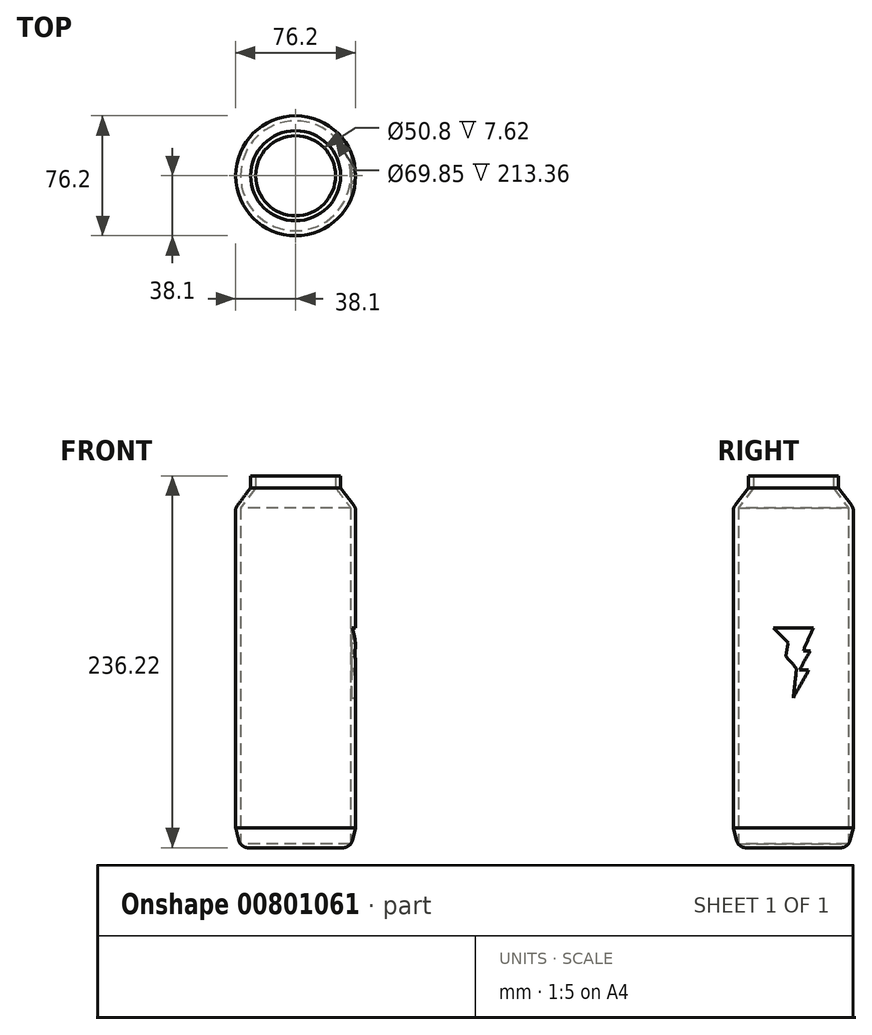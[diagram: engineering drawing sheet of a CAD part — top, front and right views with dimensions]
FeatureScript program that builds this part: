
annotation { "Feature Type Name" : "Feature", "Feature Type Description" : "" }
export const myFeature = defineFeature(function(context is Context, id is Id, definition is map)
    precondition{}
    {
        {
            var Q0;
            Q0=qCreatedBy(makeId("Top.planeOp"),FACE);
            var sketch = newSketch(context, id + "F0", { "sketchPlane" : qUnion([Q0])});
            skCircle(sketch, "E0", {"center": v(0, 0) * mm, "radius": 34.93 * mm});
            skCircle(sketch, "E1", {"center": v(0, 0) * mm, "radius": 38.1 * mm});
            skSolve(sketch);
        }
        {
            var Q0;
            Q0=makeQuery(id+"F0.imprint","IMPRINT",FACE,{"disambiguationData":[TD([[makeQuery(id+"F0.imprint","IMPRINT",EDGE,{"derivedFrom":sQuery(id+"F0.wireOp",EDGE,"E0")}),-1.0]])]});
            extrude(context, id + "F1", {"entities" : qUnion([Q0]), "depth" : 203.2 * mm, "offsetDistance" : 25.4 * mm});
        }
        {
            var Q0;
            Q0=makeQuery(id+"F0.imprint","IMPRINT",FACE,{"disambiguationData":[TD([[makeQuery(id+"F0.imprint","IMPRINT",EDGE,{"derivedFrom":sQuery(id+"F0.wireOp",EDGE,"E0")}),-1.0]])]});
            cPlane(context, id + "F2", {"entities" : qUnion([Q0]), "cplaneType" : CPlaneType.OFFSET, "offset" : 12.7 * mm, "oppositeDirection" : true, "width" : 152.4 * mm, "height" : 152.4 * mm});
        }
        {
            var Q0;
            Q0=qCreatedBy(id+"F2.planeOp",FACE);
            var sketch = newSketch(context, id + "F3", { "sketchPlane" : qUnion([Q0])});
            skCircle(sketch, "E2", {"center": v(0, 0) * mm, "radius": 34.93 * mm});
            skSolve(sketch);
        }
        {
            var Q0;
            Q0=qCreatedBy(makeId("Front.planeOp"),FACE);
            var sketch = newSketch(context, id + "F4", { "sketchPlane" : qUnion([Q0])});
            skLineSegment(sketch, "E3", {"start": v(-34.93, -12.7) * mm, "end": v(-38.1, 0) * mm});
            skLineSegment(sketch, "E4", {"start": v(-34.93, -12.7) * mm, "end": v(-34.93, 0) * mm});
            skLineSegment(sketch, "E5", {"start": v(-34.93, 0) * mm, "end": v(-38.1, 0) * mm});
            skSolve(sketch);
        }
        {
            var Q0;
            Q0=qCreatedBy(makeId("Front.planeOp"),FACE);
            var sketch = newSketch(context, id + "F5", { "sketchPlane" : qUnion([Q0])});
            skLineSegment(sketch, "E6", {"start": v(0, 0) * mm, "end": v(0, -12.7) * mm});
            skSolve(sketch);
        }
        {
            var Q0;
            Q0 = qSketchRegion(id + "F4", true);
            var Q1;
            Q1=sQuery(id+"F5.wireOp",EDGE,"E6");
            revolve(context, id + "F6", {"operationType" : NewBodyOperationType.ADD, "surfaceOperationType" : NewSurfaceOperationType.NEW, "entities" : qUnion([Q0]), "axis" : qUnion([Q1]), "revolveType" : RevolveType.FULL});
        }
        {
            var Q0;
            Q0=makeQuery(id+"F3.imprint","IMPRINT",FACE,{"disambiguationData":[TD([[makeQuery(id+"F3.imprint","IMPRINT",EDGE,{"derivedFrom":sQuery(id+"F3.wireOp",EDGE,"E2")}),1.0]])]});
            extrude(context, id + "F7", {"entities" : qUnion([Q0]), "operationType" : NewBodyOperationType.ADD, "depth" : 2.54 * mm, "offsetDistance" : 25.4 * mm});
        }
        {
            var Q0;
            Q0=makeQuery(id+"F1.opExtrude","CAP_FACE",FACE,{"disambiguationData":[OSD([sQuery(id+"F0.wireOp",EDGE,"E0"),sQuery(id+"F0.wireOp",EDGE,"E1")])],"isStart":false});
            cPlane(context, id + "F8", {"entities" : qUnion([Q0]), "cplaneType" : CPlaneType.OFFSET, "offset" : 12.7 * mm, "width" : 152.4 * mm, "height" : 152.4 * mm});
        }
        {
            var Q0;
            Q0=qCreatedBy(id+"F8.planeOp",FACE);
            var sketch = newSketch(context, id + "F9", { "sketchPlane" : qUnion([Q0])});
            skCircle(sketch, "E7", {"center": v(0, 0) * mm, "radius": 28.58 * mm});
            skSolve(sketch);
        }
        {
            var Q0;
            Q0=qCreatedBy(id+"F8.planeOp",FACE);
            var sketch = newSketch(context, id + "F10", { "sketchPlane" : qUnion([Q0])});
            skCircle(sketch, "E8", {"center": v(0, 0) * mm, "radius": 25.4 * mm});
            skSolve(sketch);
        }
        {
            var Q0;
            Q0=qCreatedBy(makeId("Front.planeOp"),FACE);
            var sketch = newSketch(context, id + "F11", { "sketchPlane" : qUnion([Q0])});
            skLineSegment(sketch, "E9", {"start": v(0, 215.9) * mm, "end": v(0, 203.2) * mm});
            skLineSegment(sketch, "E10", {"start": v(-28.58, 215.9) * mm, "end": v(-38.1, 203.2) * mm});
            skLineSegment(sketch, "E11", {"start": v(-38.1, 203.2) * mm, "end": v(-34.93, 203.2) * mm});
            skLineSegment(sketch, "E12", {"start": v(-25.4, 215.9) * mm, "end": v(-34.93, 203.2) * mm});
            skLineSegment(sketch, "E13", {"start": v(-28.58, 215.9) * mm, "end": v(-25.4, 215.9) * mm});
            skSolve(sketch);
        }
        {
            var Q0;
            Q0 = qSketchRegion(id + "F11", true);
            var Q1;
            Q1=sQuery(id+"F11.wireOp",EDGE,"E9");
            revolve(context, id + "F12", {"operationType" : NewBodyOperationType.ADD, "surfaceOperationType" : NewSurfaceOperationType.NEW, "entities" : qUnion([Q0]), "axis" : qUnion([Q1]), "revolveType" : RevolveType.FULL});
        }
        {
            var Q0;
            Q0=makeQuery(id+"F9.imprint","IMPRINT",FACE,{"disambiguationData":[TD([[makeQuery(id+"F9.imprint","IMPRINT",EDGE,{"derivedFrom":sQuery(id+"F9.wireOp",EDGE,"E7")}),1.0]])]});
            extrude(context, id + "F13", {"entities" : qUnion([Q0]), "operationType" : NewBodyOperationType.ADD, "depth" : 7.62 * mm, "offsetDistance" : 25.4 * mm});
        }
        {
            var Q0;
            Q0 = qSketchRegion(id + "F10", true);
            extrude(context, id + "F14", {"entities" : qUnion([Q0]), "operationType" : NewBodyOperationType.REMOVE, "depth" : 25.4 * mm, "offsetDistance" : 25.4 * mm});
        }
        {
            var Q0;
            Q0=makeQuery(id+"F7.boolean.opBoolean","MERGE",EDGE,{"derivedFrom":[makeQuery(id+"F6.opRevolve","SWEPT_EDGE",EDGE,{"disambiguationData":[OSD([sQuery(id+"F4.wireOp",EDGE,"E3"),sQuery(id+"F4.wireOp",EDGE,"E4")])]}),makeQuery(id+"F7.opExtrude","CAP_EDGE",EDGE,{"disambiguationData":[OSD([sQuery(id+"F3.wireOp",EDGE,"E2")])],"isStart":true})]});
            fillet(context, id + "F15", {"entities" : qUnion([Q0]), "radius" : 6.35 * mm, "tangentPropagation" : true, "allowEdgeOverflow" : false});
        }
        {
            var Q0;
            Q0=makeQuery(id+"F12.boolean.opBoolean","MERGE",EDGE,{"derivedFrom":[makeQuery(id+"F1.opExtrude","CAP_EDGE",EDGE,{"disambiguationData":[OSD([sQuery(id+"F0.wireOp",EDGE,"E1")])],"isStart":false}),makeQuery(id+"F12.opRevolve","SWEPT_EDGE",EDGE,{"disambiguationData":[OSD([sQuery(id+"F11.wireOp",EDGE,"E10"),sQuery(id+"F11.wireOp",EDGE,"E11")])]})]});
            fillet(context, id + "F16", {"entities" : qUnion([Q0]), "radius" : 5.08 * mm, "tangentPropagation" : true, "allowEdgeOverflow" : false});
        }
        {
            var Q0;
            Q0=qCreatedBy(makeId("Right.planeOp"),FACE);
            cPlane(context, id + "F17", {"entities" : qUnion([Q0]), "cplaneType" : CPlaneType.OFFSET, "offset" : 38.1 * mm, "width" : 152.4 * mm, "height" : 152.4 * mm});
        }
        {
            var Q0;
            Q0=qCreatedBy(id+"F17.planeOp",FACE);
            var sketch = newSketch(context, id + "F18", { "sketchPlane" : qUnion([Q0])});
            skLineSegment(sketch, "E14", {"start": v(-12.7, 127) * mm, "end": v(12.7, 127) * mm});
            skLineSegment(sketch, "E15", {"start": v(0, 82.55) * mm, "end": v(9.75, 100.1) * mm});
            skLineSegment(sketch, "E16", {"start": v(9.75, 100.1) * mm, "end": v(3.84, 100.1) * mm});
            skLineSegment(sketch, "E17", {"start": v(3.84, 100.1) * mm, "end": v(10.8, 112.44) * mm});
            skLineSegment(sketch, "E18", {"start": v(10.8, 112.44) * mm, "end": v(6.4, 112.44) * mm});
            skLineSegment(sketch, "E19", {"start": v(6.4, 112.44) * mm, "end": v(12.7, 127) * mm});
            skLineSegment(sketch, "E20", {"start": v(-12.7, 127) * mm, "end": v(-3.25, 117.53) * mm});
            skLineSegment(sketch, "E21", {"start": v(-3.25, 117.53) * mm, "end": v(-4.74, 108.8) * mm});
            skLineSegment(sketch, "E22", {"start": v(-4.74, 108.8) * mm, "end": v(2.07, 101.26) * mm});
            skLineSegment(sketch, "E23", {"start": v(2.07, 101.26) * mm, "end": v(0, 82.55) * mm});
            skLineSegment(sketch, "E24", {"start": v(-12.7, 127) * mm, "end": v(0, 127) * mm});
            skLineSegment(sketch, "E25", {"start": v(0, 127) * mm, "end": v(12.7, 127) * mm});
            skSolve(sketch);
        }
        {
            var Q0;
            Q0=makeQuery(id+"F18.imprint","IMPRINT",FACE,{"disambiguationData":[TD([[makeQuery(id+"F18.imprint","IMPRINT",EDGE,{"derivedFrom":sQuery(id+"F18.wireOp",EDGE,"E15")}),1.0]])]});
            extrude(context, id + "F19", {"entities" : qUnion([Q0]), "operationType" : NewBodyOperationType.REMOVE, "oppositeDirection" : true, "depth" : 2.54 * mm, "offsetDistance" : 25.4 * mm});
        }
    });
